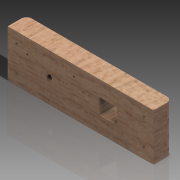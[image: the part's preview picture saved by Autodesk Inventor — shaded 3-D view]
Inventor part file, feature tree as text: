
AUTODESK INVENTOR PART (.ipt)
format: ipt  version: 2014 SP1 (Build 180222100, 222)  size: 158,720 bytes
history: native  units: mm
features: sketch x3, extrude x2, hole x1, fillet x1
ambient origin geometry x8: Origin, YZ Plane, XZ Plane, XY Plane, X Axis, Y Axis, Z Axis, Center Point
bodies: Volumenkörper1 (feature_tree)
feature tree (7):
  extrude  "Extrusion1"  Depth=45.0mm
  hole  "Bohrung1"  [1 undecoded]
  fillet  "Rundung3"  Radius=25.0mm
  extrude  "Extrusion3"  Depth=18.0mm
  sketch  "Skizze1"  dims[d0=140.0mm d1=45.0mm]
  sketch  "Skizze2"  dims[d2=18.0mm d3=0.0mm d14=10.0mm d15=25.0mm]
  sketch  "Skizze3"  dims[d16=10.0mm d17=25.0mm d18=9.0mm d19=9.0mm d20=2.0mm d21=6.0mm d22=5.0mm d23=2.0mm d24=90.0deg d25=8.0mm d26=20.594885mm d27=5.0mm d32=17.0mm d33=15.0mm d34=15.0mm d39=35.0mm d40=5.0mm d41=22.5mm d42=40.0mm d43=18.0mm d44=0.0mm]
note: 1 required parameter value undecoded (feature->parameter linkage not recoverable at this tier; creation-order binding heuristic only, values carry confidence <= 0.55)
